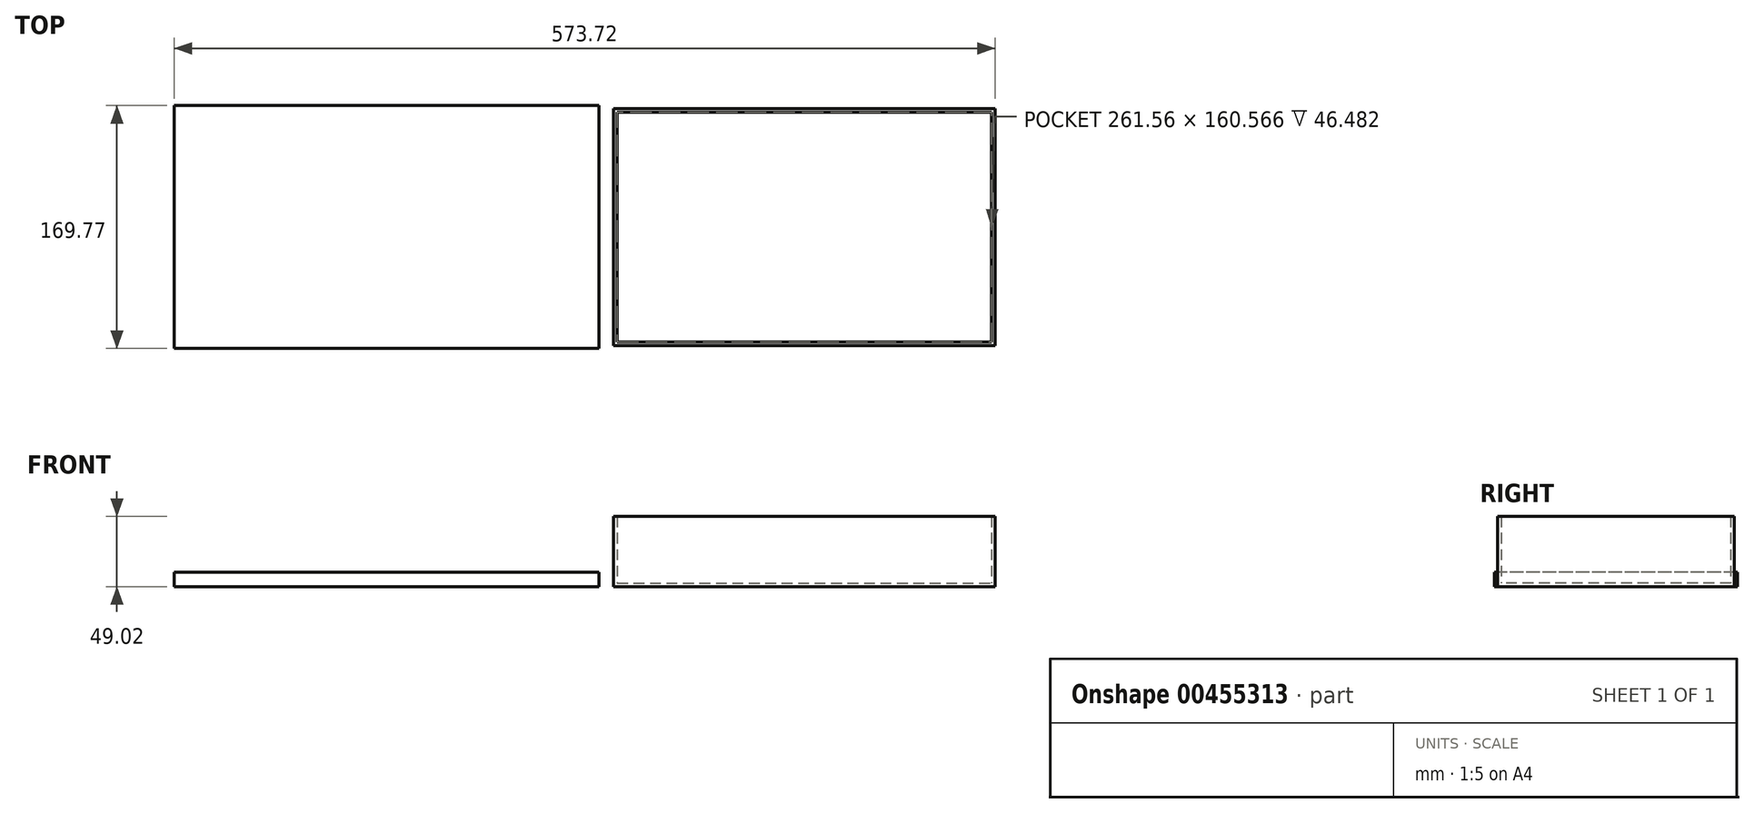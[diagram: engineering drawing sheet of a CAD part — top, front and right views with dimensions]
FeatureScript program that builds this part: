
annotation { "Feature Type Name" : "Feature", "Feature Type Description" : "" }
export const myFeature = defineFeature(function(context is Context, id is Id, definition is map)
    precondition{}
    {
        {
            var Q0;
            Q0=qCreatedBy(makeId("Top.planeOp"),FACE);
            var sketch = newSketch(context, id + "F0", { "sketchPlane" : qUnion([Q0])});
            skLineSegment(sketch, "E0.bottom", {"start": v(-147.6, 83.18) * mm, "end": v(119.04, 83.18) * mm});
            skLineSegment(sketch, "E0.top", {"start": v(-147.6, -82.47) * mm, "end": v(119.04, -82.47) * mm});
            skLineSegment(sketch, "E0.left", {"start": v(-147.6, 83.18) * mm, "end": v(-147.6, -82.47) * mm});
            skLineSegment(sketch, "E0.right", {"start": v(119.04, 83.18) * mm, "end": v(119.04, -82.47) * mm});
            skSolve(sketch);
        }
        {
            var Q0;
            Q0 = qSketchRegion(id + "F0", true);
            extrude(context, id + "F1", {"entities" : qUnion([Q0]), "depth" : 49.02 * mm});
        }
        {
            var Q0;
            Q0=qCreatedBy(makeId("Top.planeOp"),FACE);
            var sketch = newSketch(context, id + "F2", { "sketchPlane" : qUnion([Q0])});
            skLineSegment(sketch, "E1.bottom", {"start": v(-157.88, 85.3) * mm, "end": v(-454.68, 85.3) * mm});
            skLineSegment(sketch, "E1.top", {"start": v(-157.88, -84.46) * mm, "end": v(-454.68, -84.46) * mm});
            skLineSegment(sketch, "E1.left", {"start": v(-157.88, 85.3) * mm, "end": v(-157.88, -84.46) * mm});
            skLineSegment(sketch, "E1.right", {"start": v(-454.68, 85.3) * mm, "end": v(-454.68, -84.46) * mm});
            skSolve(sketch);
        }
        {
            var Q0;
            Q0 = qSketchRegion(id + "F2", true);
            extrude(context, id + "F3", {"entities" : qUnion([Q0]), "depth" : 10.16 * mm});
        }
        {
            var Q0;
            Q0=makeQuery(id+"F1.opExtrude","CAP_FACE",FACE,{"disambiguationData":[OSD([sQuery(id+"F0.wireOp",EDGE,"E0.bottom"),sQuery(id+"F0.wireOp",EDGE,"E0.top"),sQuery(id+"F0.wireOp",EDGE,"E0.left"),sQuery(id+"F0.wireOp",EDGE,"E0.right")])],"isStart":false});
            shell(context, id + "F4", {"entities" : qUnion([Q0]), "thickness" : 2.54 * mm});
        }
    });
